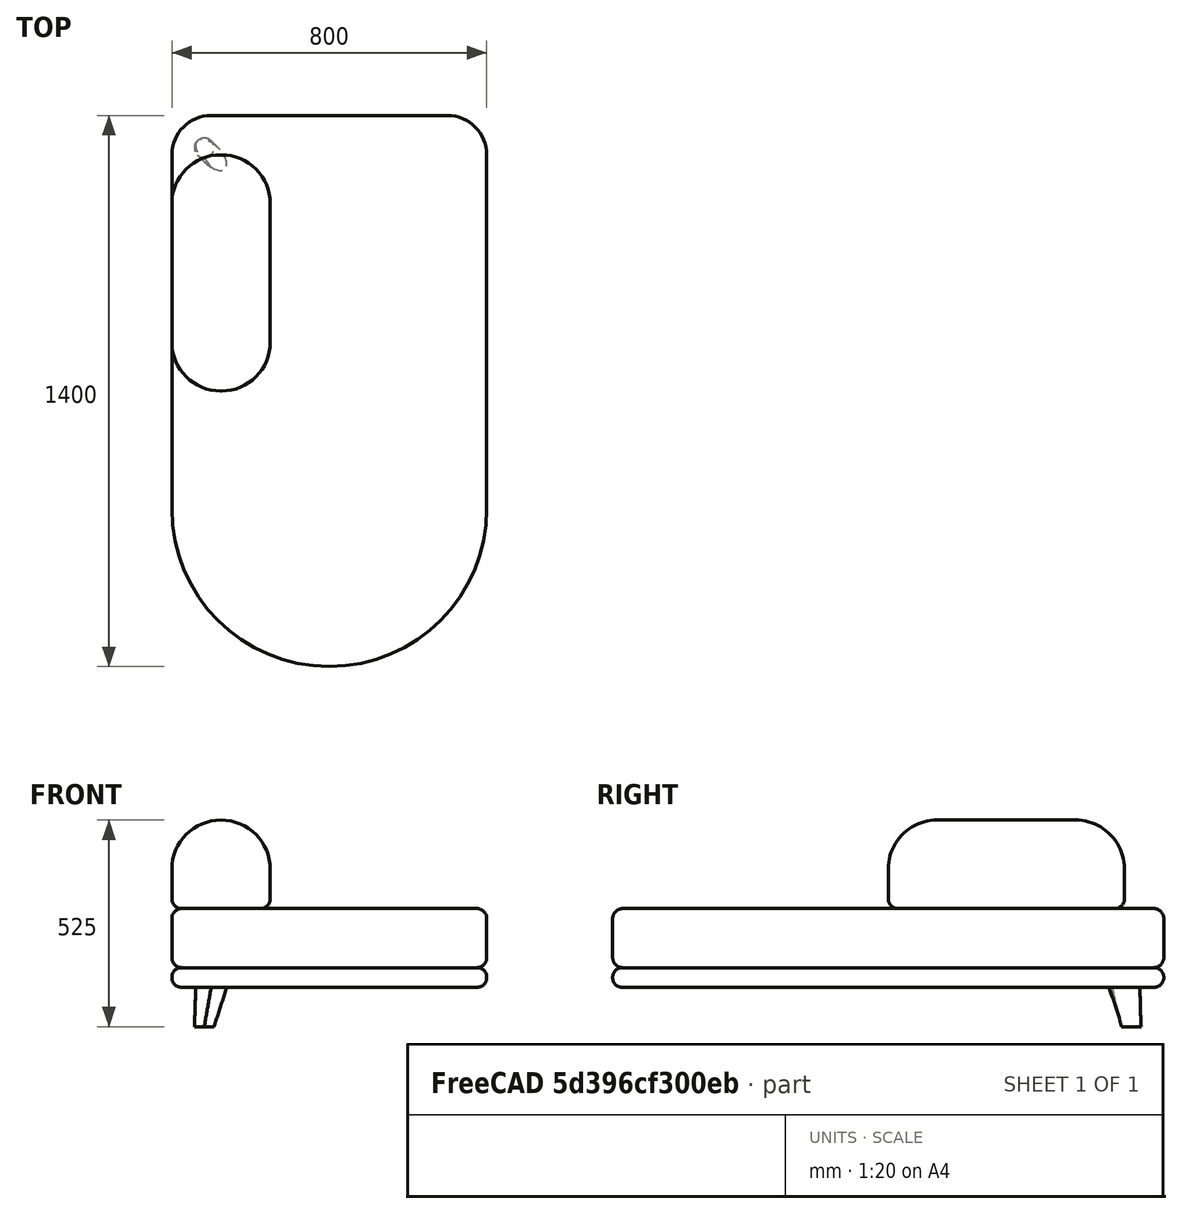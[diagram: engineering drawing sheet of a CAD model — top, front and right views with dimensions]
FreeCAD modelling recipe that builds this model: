
FCSTD DOCUMENT  (FreeCAD 1.0R39319 (Git))
Label: Drawing room Sofa lounger
License: All rights reserved
objects: App::Link×7, App::FeaturePython×7, Sketcher::SketchObject×5, PartDesign::Fillet×4, PartDesign::Body×4, PartDesign::Pad×3, PartDesign::Plane×1, PartDesign::AdditiveLoft×1, Assembly::JointGroup×1, Assembly::AssemblyObject×1
note: 39 computed .brp shape members not serialized (recipe doc carries the construction recipe); baked Part::Feature solids carry a one-line shape summary decoded from their .brp

FEATURE [Sketcher::SketchObject] Sketch
  ArcFitTolerance = 1e-06
  AttachmentSupport = -> [XY_Plane]
  FullyConstrained = true
  MakeInternals = false
  MapMode = 5
  sketch-geometry (6):
    g0: LineSegment StartX=100 StartY=0 StartZ=0 EndX=700 EndY=0 EndZ=0
    g1: ArcOfCircle CenterX=700 CenterY=-100 CenterZ=0 NormalX=0 NormalY=0 NormalZ=1 AngleXU=0 Radius=100 StartAngle=1e-16 EndAngle=1.5708
    g2: LineSegment StartX=800 StartY=-100 StartZ=0 EndX=800 EndY=-1000 EndZ=0
    g3: ArcOfCircle CenterX=400 CenterY=-1000 CenterZ=0 NormalX=0 NormalY=0 NormalZ=1 AngleXU=0 Radius=400 StartAngle=3.14159 EndAngle=6.28319
    g4: LineSegment StartX=0 StartY=-1000 StartZ=0 EndX=0 EndY=-100 EndZ=0
    g5: ArcOfCircle CenterX=100 CenterY=-100 CenterZ=0 NormalX=0 NormalY=0 NormalZ=1 AngleXU=0 Radius=100 StartAngle=1.5708 EndAngle=3.14159
  constraints (15):
    c: PointOnObject(g0,g-1)
    c: Horizontal(g0)
    c: Tangent(g0,g1) = 1.5708
    c: Tangent(g1,g2) = 1.5708
    c: Tangent(g2,g3) = 1.5708
    c: PointOnObject(g3,g-2)
    c: Tangent(g3,g4) = 1.5708
    c: Tangent(g4,g5) = 1.5708
    c: Radius(g1) = 100
    c: Radius(g5) = 100
    c: Vertical(g4)
    c: Vertical(g2)
    c: Tangent(g5,g0) = 1.5708
    c: DistanceX(g0,g0) = 600
    c: DistanceY(g2,g2) = 900
FEATURE [PartDesign::Pad] Pad
  Direction = (0,0,1)
  Length = 50
  Length2 = 10
  Profile = -> Sketch
  ReferenceAxis = -> Sketch [N_Axis]
  Refine = true
  Suppressed = false
  Type = 0
FEATURE [Sketcher::SketchObject] Sketch001
  ArcFitTolerance = 1e-06
  AttachmentSupport = -> [XY_Plane001]
  FullyConstrained = true
  MakeInternals = false
  MapMode = 5
  sketch-geometry (7):
    g0: LineSegment StartX=0 StartY=-100 StartZ=0 EndX=0 EndY=-1000 EndZ=0
    g1: LineSegment StartX=800 StartY=-1000 StartZ=0 EndX=800 EndY=-100 EndZ=0
    g2: LineSegment StartX=700 StartY=0 StartZ=0 EndX=100 EndY=0 EndZ=0
    g3: ArcOfCircle CenterX=100 CenterY=-100 CenterZ=0 NormalX=0 NormalY=0 NormalZ=1 AngleXU=0 Radius=100 StartAngle=1.5708 EndAngle=3.14159
    g4: ArcOfCircle CenterX=700 CenterY=-100 CenterZ=0 NormalX=0 NormalY=0 NormalZ=1 AngleXU=0 Radius=100 StartAngle=0 EndAngle=1.5708
    g5: GeomPoint [constr] X=0 Y=0 Z=0
    g6: ArcOfCircle CenterX=400 CenterY=-1000 CenterZ=0 NormalX=0 NormalY=0 NormalZ=1 AngleXU=0 Radius=400 StartAngle=3.14159 EndAngle=6.28319
  constraints (16):
    c: Tangent(g0,g3) = -1.5708
    c: Tangent(g1,g4) = -1.5708
    c: Tangent(g2,g4) = -1.5708
    c: Tangent(g2,g3) = -1.5708
    c: Vertical(g0)
    c: Vertical(g1)
    c: Horizontal(g2)
    c: PointOnObject(g5,g0)
    c: PointOnObject(g5,g2)
    c: Distance(g0,g1) = 800
    c: Coincident(g5,g-1)
    c: Tangent(g6,g1) = -1.5708
    c: Tangent(g6,g0) = -1.5708
    c: Radius(g4) = 100
    c: Radius(g3) = 100
    c: Distance(g1) = 900
FEATURE [PartDesign::Pad] Pad001
  Direction = (0,0,1)
  Length = 150
  Length2 = 10
  Profile = -> Sketch001
  ReferenceAxis = -> Sketch001 [N_Axis]
  Refine = true
  Suppressed = false
  Type = 0
FEATURE [PartDesign::Fillet] Fillet
  Base = -> Pad001
  BaseFeature = -> Pad001
  Radius = 25
  Refine = true
  SupportTransform = false
  Suppressed = false
  UseAllEdges = true
FEATURE [PartDesign::Body] Body001  label="Cushion"
  AllowCompound = false
  Group = -> [Sketch001,Pad001,Fillet]
  Origin = -> Origin001
  Placement = pos=(0,0,50) rot=(0,0,1;0rad)
  Tip = -> Fillet
FEATURE [PartDesign::Fillet] Fillet001
  Base = -> Pad [?Face10]
  BaseFeature = -> Pad
  Radius = 24
  Refine = true
  SupportTransform = false
  Suppressed = false
  UseAllEdges = true
FEATURE [PartDesign::Body] Body  label="Base"
  AllowCompound = false
  Group = -> [Sketch,Pad,Fillet001]
  Origin = -> Origin
  Tip = -> Fillet001
FEATURE [Sketcher::SketchObject] Sketch002
  ArcFitTolerance = 1e-06
  AttachmentSupport = -> [XZ_Plane002]
  FullyConstrained = true
  MakeInternals = false
  MapMode = 5
  Placement = pos=(0,0,0) rot=(1,0,0;1.5708rad)
  sketch-geometry (5):
    g0: LineSegment StartX=0 StartY=0 StartZ=0 EndX=250 EndY=0 EndZ=0
    g1: LineSegment StartX=250 StartY=0 StartZ=0 EndX=250 EndY=100 EndZ=0
    g2: LineSegment [constr] StartX=250 StartY=100 StartZ=0 EndX=0 EndY=100 EndZ=0
    g3: LineSegment StartX=0 StartY=100 StartZ=0 EndX=0 EndY=0 EndZ=0
    g4: ArcOfCircle CenterX=125 CenterY=100 CenterZ=0 NormalX=0 NormalY=0 NormalZ=1 AngleXU=0 Radius=125 StartAngle=0 EndAngle=3.14159
  constraints (14):
    c: Coincident(g0,g1)
    c: Coincident(g1,g2)
    c: Coincident(g2,g3)
    c: Coincident(g3,g0)
    c: Horizontal(g0)
    c: Horizontal(g2)
    c: Vertical(g1)
    c: Vertical(g3)
    c: Distance(g1,g3) = 250
    c: Distance(g0,g2) = 100
    c: Coincident(g0,g-1)
    c: Coincident(g4,g2)
    c: Coincident(g4,g1)
    c: PointOnObject(g4,g2)
FEATURE [PartDesign::Pad] Pad002
  Direction = (0,-1,2e-16)
  Length = 600
  Length2 = 10
  Placement = pos=(0,0,0) rot=(1,0,0;1.5708rad)
  Profile = -> Sketch002
  ReferenceAxis = -> Sketch002 [N_Axis]
  Refine = true
  Suppressed = false
  Type = 0
FEATURE [PartDesign::Fillet] Fillet002
  Base = -> Pad002 [Edge9,Edge10]
  BaseFeature = -> Pad002
  Placement = pos=(0,0,0) rot=(1,0,0;1.5708rad)
  Radius = 124
  Refine = true
  SupportTransform = false
  Suppressed = false
  UseAllEdges = false
FEATURE [PartDesign::Fillet] Fillet003
  Base = -> Fillet002 [Face1]
  BaseFeature = -> Fillet002
  Placement = pos=(0,0,0) rot=(1,0,0;1.5708rad)
  Radius = 25
  Refine = true
  SupportTransform = false
  Suppressed = false
  UseAllEdges = true
FEATURE [PartDesign::Body] Body002  label="Backrest"
  AllowCompound = false
  Group = -> [Sketch002,Pad002,Fillet002,Fillet003]
  Origin = -> Origin002
  Placement = pos=(0,-100,200) rot=(0,0,1;0rad)
  Tip = -> Fillet003
FEATURE [Sketcher::SketchObject] Sketch003
  ArcFitTolerance = 1e-06
  AttachmentSupport = -> [XY_Plane003]
  FullyConstrained = true
  MakeInternals = false
  MapMode = 5
  sketch-geometry (5):
    g0: Ellipse CenterX=0 CenterY=0 CenterZ=0 NormalX=0 NormalY=0 NormalZ=1 MajorRadius=50 MinorRadius=25 AngleXU=-2.35619
    g1: LineSegment [constr] StartX=-35.3553 StartY=-35.3553 StartZ=0 EndX=35.3553 EndY=35.3553 EndZ=0
    g2: LineSegment [constr] StartX=17.6777 StartY=-17.6777 StartZ=0 EndX=-17.6777 EndY=17.6777 EndZ=0
    g3: GeomPoint [constr] X=-30.6186 Y=-30.6186 Z=0
    g4: GeomPoint [constr] X=30.6186 Y=30.6186 Z=0
  constraints (5):
    c: InternalAlignment(g1-g4 -> g0) x4
    c: Distance(g0,g1) = 50
    c: Angle(g1) = 0.785398
    c: Distance(g0,g2) = 25
    c: Coincident(g0,g-1)
FEATURE [PartDesign::Plane] DatumPlane
  AttachmentOffset = pos=(0,0,-100) rot=(0,0,1;0rad)
  AttachmentSupport = -> [Sketch003]
  Length = 98.636
  MapMode = 2
  Placement = pos=(0,0,-100) rot=(0,0,1;0rad)
  ResizeMode = 0
  Width = 98.6418
FEATURE [Sketcher::SketchObject] Sketch004
  ArcFitTolerance = 1e-06
  AttachmentSupport = -> [DatumPlane]
  FullyConstrained = true
  MakeInternals = false
  MapMode = 5
  Placement = pos=(0,0,-100) rot=(0,0,1;0rad)
  sketch-geometry (2):
    g0: Circle CenterX=-17.6777 CenterY=-17.6777 CenterZ=0 NormalX=0 NormalY=0 NormalZ=1 AngleXU=0 Radius=25
    g1: LineSegment [constr] StartX=-17.6777 StartY=-17.6777 StartZ=0 EndX=2.4e-15 EndY=4.5e-15 EndZ=0
  constraints (5):
    c: Diameter(g0) = 50
    c: Coincident(g1,g0)
    c: Coincident(g1,g-1)
    c: Angle(g1,g-1) = 2.35619
    c: PointOnObject(g1,g0)
FEATURE [PartDesign::AdditiveLoft] AdditiveLoft
  Closed = false
  Profile = -> Sketch003
  Refine = true
  Ruled = false
  Sections = -> [Sketch004]
  Suppressed = false
FEATURE [PartDesign::Body] Body003  label="Legs"
  AllowCompound = false
  Group = -> [Sketch003,DatumPlane,Sketch004,AdditiveLoft]
  Origin = -> Origin003
  Placement = pos=(100,-100,0) rot=(0,0,1;-1.5708rad)
  Tip = -> AdditiveLoft
FEATURE [App::Link] Base  label="Base001"
  LinkedObject = -> Body
FEATURE [App::FeaturePython] GroundedJoint  # Assembly grounded joint (typed FeaturePython)
  ObjectToGround = -> Base
FEATURE [App::Link] Cushion  label="Cushion001"
  LinkPlacement = pos=(-1.83e-14,0.0588181,50) rot=(0,0,1;0rad)
  LinkedObject = -> Body001
  Placement = pos=(-1.83e-14,0.0588181,50) rot=(0,0,1;0rad)
FEATURE [App::Link] Backrest  label="Backrest001"
  LinkPlacement = pos=(700,-39.0404,200) rot=(0,0,-1;1.5708rad)
  LinkedObject = -> Body002
  Placement = pos=(700,-39.0404,200) rot=(0,0,-1;1.5708rad)
FEATURE [App::Link] Legs  label="Legs001"
  LinkPlacement = pos=(700,-364.04,0) rot=(0,0,1;3.14159rad)
  LinkedObject = -> Body003
  Placement = pos=(700,-364.04,0) rot=(0,0,1;3.14159rad)
FEATURE [App::Link] Legs001  label="Legs002"
  LinkPlacement = pos=(100,-964.04,0) rot=(0,0,1;0rad)
  LinkedObject = -> Body003
  Placement = pos=(100,-964.04,0) rot=(0,0,1;0rad)
FEATURE [App::Link] Legs002  label="Legs003"
  LinkPlacement = pos=(700,-964.04,0) rot=(0,0,1;1.5708rad)
  LinkedObject = -> Body003
  Placement = pos=(700,-964.04,0) rot=(0,0,1;1.5708rad)
FEATURE [App::Link] Legs003  label="Legs004"
  LinkPlacement = pos=(100,-364.04,0) rot=(0,0,-1;1.5708rad)
  LinkedObject = -> Body003
  Placement = pos=(100,-364.04,0) rot=(0,0,-1;1.5708rad)
FEATURE [App::FeaturePython] Joint  label="Fixed"  # Assembly joint (typed FeaturePython)
  Activated = true
  AngleMax = 0
  AngleMin = 0
  Detach1 = false
  Detach2 = false
  Distance = 0
  Distance2 = 0
  EnableAngleMax = false
  EnableAngleMin = false
  EnableLengthMax = false
  EnableLengthMin = false
  JointType = 0 (Fixed)
  LengthMax = 0
  LengthMin = 0
  Placement1 = pos=(400,-664.04,50) rot=(0,0,1;0rad)
  Placement2 = pos=(400,-664.099,0) rot=(0,0,1;0rad)
  Reference1 = -> Assembly [Base.Face11,Base.Face11]
  Reference2 = -> Assembly [Cushion.Face9,Cushion.Face9]
FEATURE [App::FeaturePython] Joint001  label="Fixed001"  # Assembly joint (typed FeaturePython)
  Activated = true
  AngleMax = 0
  AngleMin = 0
  Detach1 = false
  Detach2 = false
  Distance = 0
  Distance2 = 0
  EnableAngleMax = false
  EnableAngleMin = false
  EnableLengthMax = false
  EnableLengthMin = false
  JointType = 0 (Fixed)
  LengthMax = 0
  LengthMin = 0
  Offset1 = pos=(500,0,0) rot=(0,0,1;1.5708rad)
  Placement1 = pos=(625,-300,5.68e-14) rot=(0,0,1;1.5708rad)
  Placement2 = pos=(400,-664.099,150) rot=(0,0,1;0rad)
  Reference1 = -> Assembly [Backrest.Face1,Backrest.Face1]
  Reference2 = -> Assembly [Cushion.Face11,Cushion.Face11]
FEATURE [App::FeaturePython] Joint002  label="Fixed002"  # Assembly joint (typed FeaturePython)
  Activated = true
  AngleMax = 0
  AngleMin = 0
  Detach1 = false
  Detach2 = false
  Distance = 0
  Distance2 = 0
  EnableAngleMax = false
  EnableAngleMin = false
  EnableLengthMax = false
  EnableLengthMin = false
  JointType = 0 (Fixed)
  LengthMax = 0
  LengthMin = 0
  Offset1 = pos=(300,300,0) rot=(0,0,1;0rad)
  Offset2 = pos=(0,0,0) rot=(0,0,1;3.14159rad)
  Placement1 = pos=(700,-364.04,0) rot=(0,0,1;0rad)
  Placement2 = pos=(0,0,0) rot=(0,0,1;3.14159rad)
  Reference1 = -> Assembly [Base.Face9,Base.Face9]
  Reference2 = -> Assembly [Legs.Face1,Legs.Face1]
FEATURE [App::FeaturePython] Joint003  label="Fixed003"  # Assembly joint (typed FeaturePython)
  Activated = true
  AngleMax = 0
  AngleMin = 0
  Detach1 = false
  Detach2 = false
  Distance = 0
  Distance2 = 0
  EnableAngleMax = false
  EnableAngleMin = false
  EnableLengthMax = false
  EnableLengthMin = false
  JointType = 0 (Fixed)
  LengthMax = 0
  LengthMin = 0
  Offset1 = pos=(-300,-300,0) rot=(0,0,1;0rad)
  Placement1 = pos=(100,-964.04,0) rot=(0,0,1;0rad)
  Reference1 = -> Assembly [Base.Face9,Base.Face9]
  Reference2 = -> Assembly [Legs001.Face1,Legs001.Face1]
FEATURE [App::FeaturePython] Joint004  label="Fixed004"  # Assembly joint (typed FeaturePython)
  Activated = true
  AngleMax = 0
  AngleMin = 0
  Detach1 = false
  Detach2 = false
  Distance = 0
  Distance2 = 0
  EnableAngleMax = false
  EnableAngleMin = false
  EnableLengthMax = false
  EnableLengthMin = false
  JointType = 0 (Fixed)
  LengthMax = 0
  LengthMin = 0
  Offset1 = pos=(300,-300,0) rot=(0,0,1;1.5708rad)
  Placement1 = pos=(700,-964.04,0) rot=(0,0,1;1.5708rad)
  Reference1 = -> Assembly [Base.Face9,Base.Face9]
  Reference2 = -> Assembly [Legs002.Face1,Legs002.Face1]
FEATURE [App::FeaturePython] Joint005  label="Fixed005"  # Assembly joint (typed FeaturePython)
  Activated = true
  AngleMax = 0
  AngleMin = 0
  Detach1 = false
  Detach2 = false
  Distance = 0
  Distance2 = 0
  EnableAngleMax = false
  EnableAngleMin = false
  EnableLengthMax = false
  EnableLengthMin = false
  JointType = 0 (Fixed)
  LengthMax = 0
  LengthMin = 0
  Offset1 = pos=(-300,300,0) rot=(0,0,-1;1.5708rad)
  Placement1 = pos=(100,-364.04,0) rot=(0,0,-1;1.5708rad)
  Reference1 = -> Assembly [Base.Face9,Base.Face9]
  Reference2 = -> Assembly [Legs003.Face1,Legs003.Face1]
FEATURE [Assembly::JointGroup] Joints
  Group = -> [GroundedJoint,Joint,Joint001,Joint002,Joint003,Joint004,Joint005]
FEATURE [Assembly::AssemblyObject] Assembly
  Group = -> [Joints,Base,GroundedJoint,Cushion,Backrest,Legs,Legs001,Legs002,Legs003,Joint,Joint001,Joint002,Joint003,Joint004,Joint005]
  Origin = -> Origin004
  Type = Assembly
